# Revit family: Haworth_ImprovSide_Stool_LegBase
name_source: partatom
category: Furniture
revit_build: Autodesk Revit 2018 (Build: 20170223_1515(x64)
units: mm (PartAtom-declared; Revit-internal decimal feet)

## family parameters
Always vertical = Yes
Cut with Voids When Loaded = No
OmniClass Number = 23.40.20.00
OmniClass Title = General Furniture and Specialties
Room Calculation Point = No
Shared = No
Work Plane-Based = No

## types (1)
- Wood Back
    Actual Depth = 1' - 10 11/16"
    Actual Height = 3' - 5 1/4"
    Actual Width = 1' - 8 13/16"
    Arm Cap Finish = Haworth _ Polymer _ Fog
    Assembly Code = E2020200
    Back Finish = Haworth _ Wood _ Beech
    Depth = 23 in.
    Description = Haworth - Improv Side - Stool - Leg Base
    Frame Finish = Haworth _ Paint _ Graphite
    Front Leg Height = 2' - 8 1/2"
    Front Void Offset = -0' - 0 1/4"
    Height = 41.25 in.
    Manufacturer = Haworth
    Model = Haworth - Improv Side - Stool - Leg Base
    Revision = 2
    Seat Finish = Haworth _ Fabric _ Tellure _ Tomato 3A-43
    Size = Verify Final Dim. w/ Haworth
    Sustainability Info = http://www.haworth.com
    URL = http://haworth.com
    URL - Product = http://www.haworth.com
    Upholstered Back = No
    Warranty = http://www.haworth.com
    Width = 22 in.
    With Arms = Yes
    Without Arms = No
    Wood Back = Yes

## geometry (parser evidence)
native form markers: Sweep x2
no freeform markers — native parametric forms only
